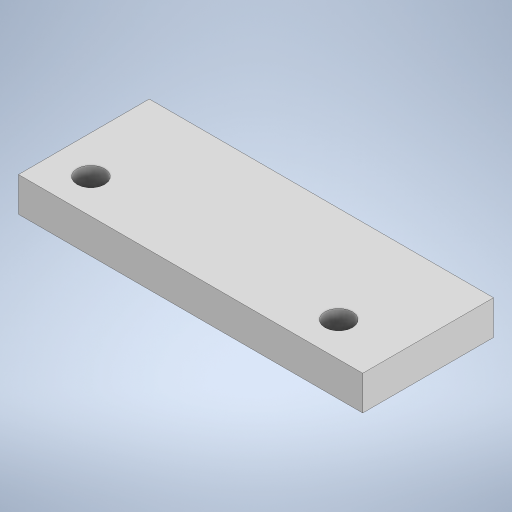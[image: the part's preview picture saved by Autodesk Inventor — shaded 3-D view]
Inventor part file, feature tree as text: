
AUTODESK INVENTOR PART (.ipt)
format: ipt  version: 2023.2 (Build 272271000, 271)  size: 210,432 bytes
history: native  units: mm
features: extrude x1, sketch x1
ambient origin geometry x8: Origin, YZ Plane, XZ Plane, XY Plane, X Axis, Y Axis, Z Axis, Center Point
bodies: Solid1 (feature_tree)
feature tree (2):
  extrude  "Extrusion1"  Depth=19.0mm
  sketch  "Sketch1"  dims[d0=50.0mm d1=19.0mm d2=4.0mm d3=4.0mm d4=36.0mm d5=5.0mm d6=5.0mm d7=0.0mm]
